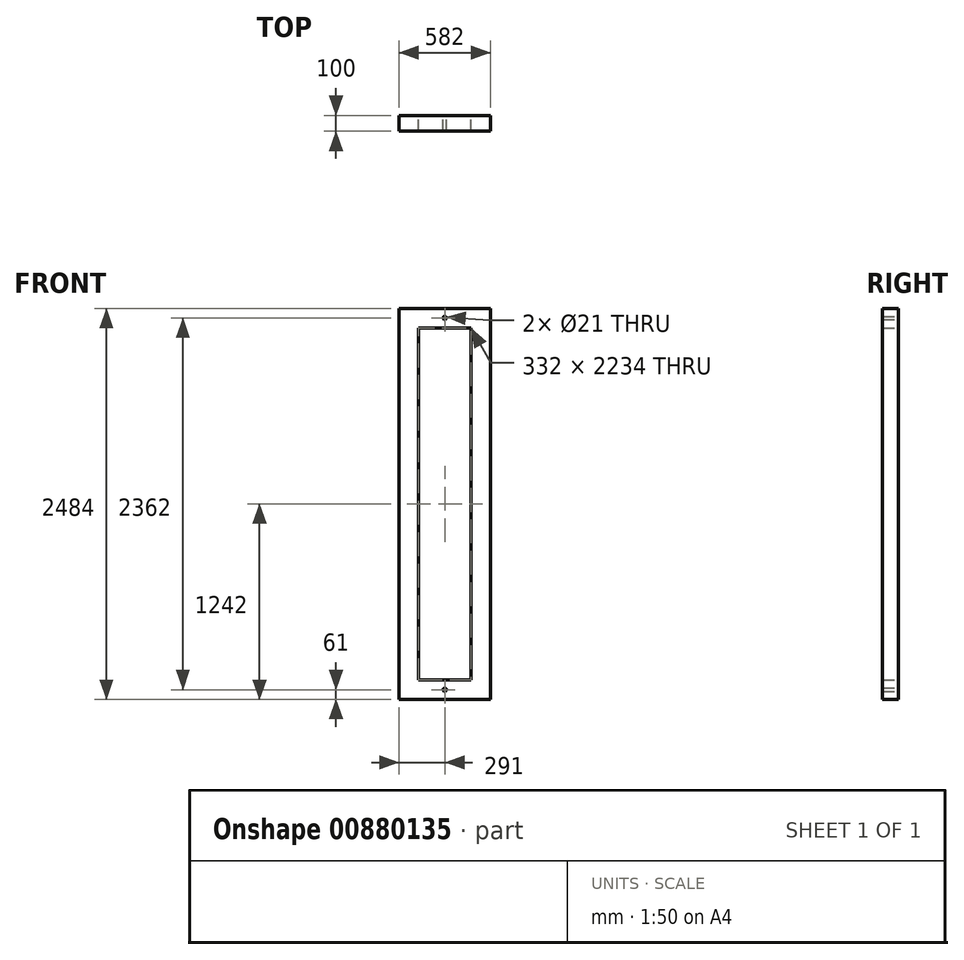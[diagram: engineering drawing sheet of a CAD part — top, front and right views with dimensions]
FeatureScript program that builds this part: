
annotation { "Feature Type Name" : "Feature", "Feature Type Description" : "" }
export const myFeature = defineFeature(function(context is Context, id is Id, definition is map)
    precondition{}
    {
        {
            var Q0;
            Q0=qCreatedBy(makeId("Front.planeOp"),FACE);
            var sketch = newSketch(context, id + "F0", { "sketchPlane" : qUnion([Q0])});
            skLineSegment(sketch, "E0", {"start": v(0, 0) * mm, "end": v(-582, 0) * mm});
            skLineSegment(sketch, "E1", {"start": v(-582, 0) * mm, "end": v(-582, 2484) * mm});
            skLineSegment(sketch, "E2", {"start": v(-582, 2484) * mm, "end": v(0, 2484) * mm});
            skLineSegment(sketch, "E3", {"start": v(0, 2484) * mm, "end": v(0, 0) * mm});
            skLineSegment(sketch, "E4", {"start": v(-582, 0) * mm, "end": v(-582, 125) * mm});
            skLineSegment(sketch, "E5", {"start": v(-582, 125) * mm, "end": v(-457, 125) * mm});
            skLineSegment(sketch, "E6", {"start": v(-457, 125) * mm, "end": v(0, 125) * mm});
            skLineSegment(sketch, "E7", {"start": v(0, 125) * mm, "end": v(-125, 125) * mm});
            skLineSegment(sketch, "E8", {"start": v(-582, 2484) * mm, "end": v(-582, 2359) * mm});
            skLineSegment(sketch, "E9", {"start": v(-582, 2359) * mm, "end": v(0, 2359) * mm});
            skLineSegment(sketch, "E10", {"start": v(0, 2359) * mm, "end": v(-125, 2359) * mm});
            skLineSegment(sketch, "E11", {"start": v(-582, 2359) * mm, "end": v(-457, 2359) * mm});
            skLineSegment(sketch, "E12", {"start": v(-457, 2359) * mm, "end": v(-457, 125) * mm});
            skLineSegment(sketch, "E13", {"start": v(-125, 125) * mm, "end": v(-125, 2359) * mm});
            skSolve(sketch);
        }
        {
            var Q0;
            Q0 = qSketchRegion(id + "F0", true);
            extrude(context, id + "F1", {"entities" : qUnion([Q0]), "depth" : 100 * mm, "offsetDistance" : 25 * mm});
        }
        {
            var Q0;
            Q0=makeQuery(id+"F1.opExtrude","CAP_FACE",FACE,{"disambiguationData":[OSD([sQuery(id+"F0.wireOp",EDGE,"E0"),sQuery(id+"F0.wireOp",EDGE,"E1"),sQuery(id+"F0.wireOp",EDGE,"E2"),sQuery(id+"F0.wireOp",EDGE,"E3"),sQuery(id+"F0.wireOp",EDGE,"E6"),sQuery(id+"F0.wireOp",EDGE,"E9"),sQuery(id+"F0.wireOp",EDGE,"E12"),sQuery(id+"F0.wireOp",EDGE,"E13")])],"isStart":true});
            var sketch = newSketch(context, id + "F2", { "sketchPlane" : qUnion([Q0])});
            skLineSegment(sketch, "E14", {"start": v(291, 2484) * mm, "end": v(291, 2423) * mm});
            skCircle(sketch, "E15", {"center": v(291, 2423) * mm, "radius": 10.5 * mm});
            skLineSegment(sketch, "E16", {"start": v(291, 0) * mm, "end": v(291, 61) * mm});
            skCircle(sketch, "E17", {"center": v(291, 61) * mm, "radius": 10.5 * mm});
            skSolve(sketch);
        }
        {
            var Q0;
            Q0 = qSketchRegion(id + "F2", true);
            extrude(context, id + "F3", {"entities" : qUnion([Q0]), "operationType" : NewBodyOperationType.REMOVE, "endBound" : BoundingType.THROUGH_ALL, "oppositeDirection" : true, "depth" : 25 * mm, "offsetDistance" : 25 * mm});
        }
    });
